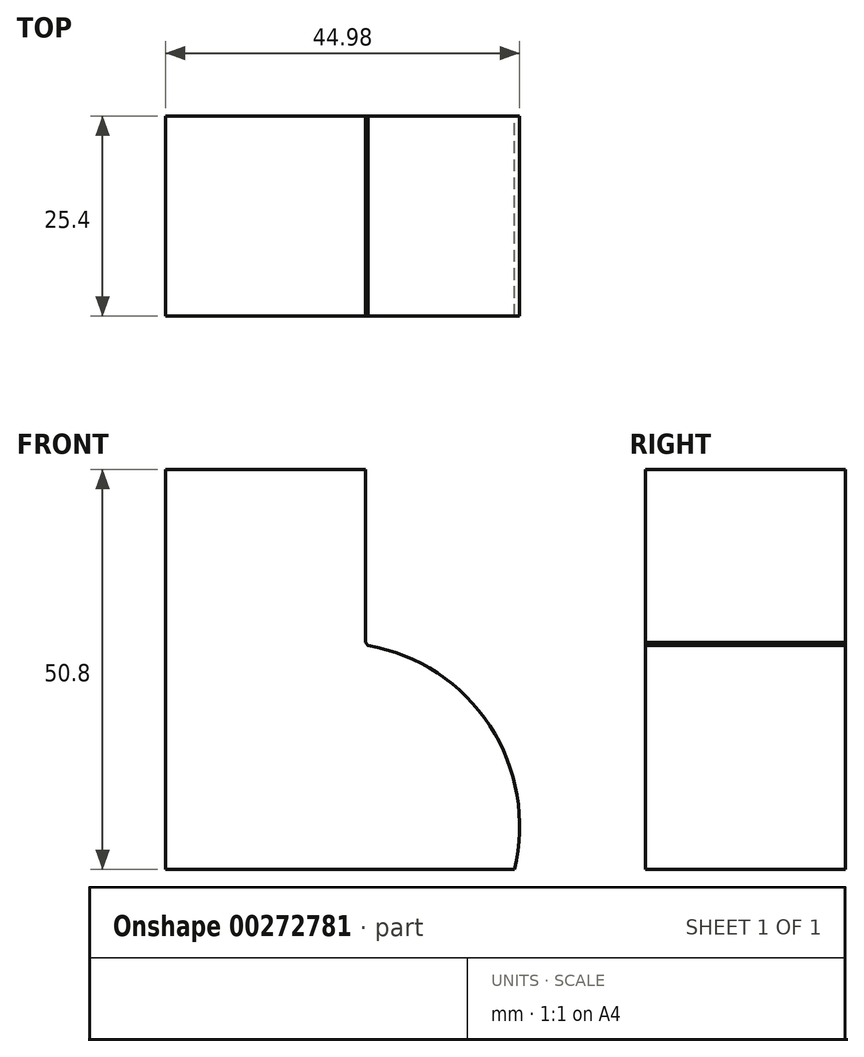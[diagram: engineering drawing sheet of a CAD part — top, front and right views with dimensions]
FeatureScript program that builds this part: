
annotation { "Feature Type Name" : "Feature", "Feature Type Description" : "" }
export const myFeature = defineFeature(function(context is Context, id is Id, definition is map)
    precondition{}
    {
        {
            var Q0;
            Q0=qCreatedBy(makeId("Front.planeOp"),FACE);
            var sketch = newSketch(context, id + "F0", { "sketchPlane" : qUnion([Q0])});
            skLineSegment(sketch, "E0", {"start": v(-67.8, 50.8) * mm, "end": v(-67.8, 0) * mm});
            skLineSegment(sketch, "E1", {"start": v(-67.8, 0) * mm, "end": v(-23.49, 0) * mm});
            skLineSegment(sketch, "E2", {"start": v(-67.8, 50.8) * mm, "end": v(-42.4, 50.8) * mm});
            skLineSegment(sketch, "E3", {"start": v(-42.4, 50.8) * mm, "end": v(-42.4, 28.86) * mm});
            skArc(sketch, "E4", {"start": v(-23.49, 0) * mm, "mid": v(-26.59, 18.25) * mm, "end": v(-42.05, 28.44) * mm});
            skLineSegment(sketch, "E5", {"start": v(-42.05, 28.44) * mm, "end": v(-42.4, 28.86) * mm});
            skSolve(sketch);
        }
        {
            var Q0;
            Q0=makeQuery(id+"F0.imprint","IMPRINT",FACE,{"disambiguationData":[TD([[makeQuery(id+"F0.imprint","IMPRINT",EDGE,{"derivedFrom":sQuery(id+"F0.wireOp",EDGE,"E0")}),1.0]])]});
            extrude(context, id + "F1", {"entities" : qUnion([Q0]), "depth" : 25.4 * mm});
        }
    });
